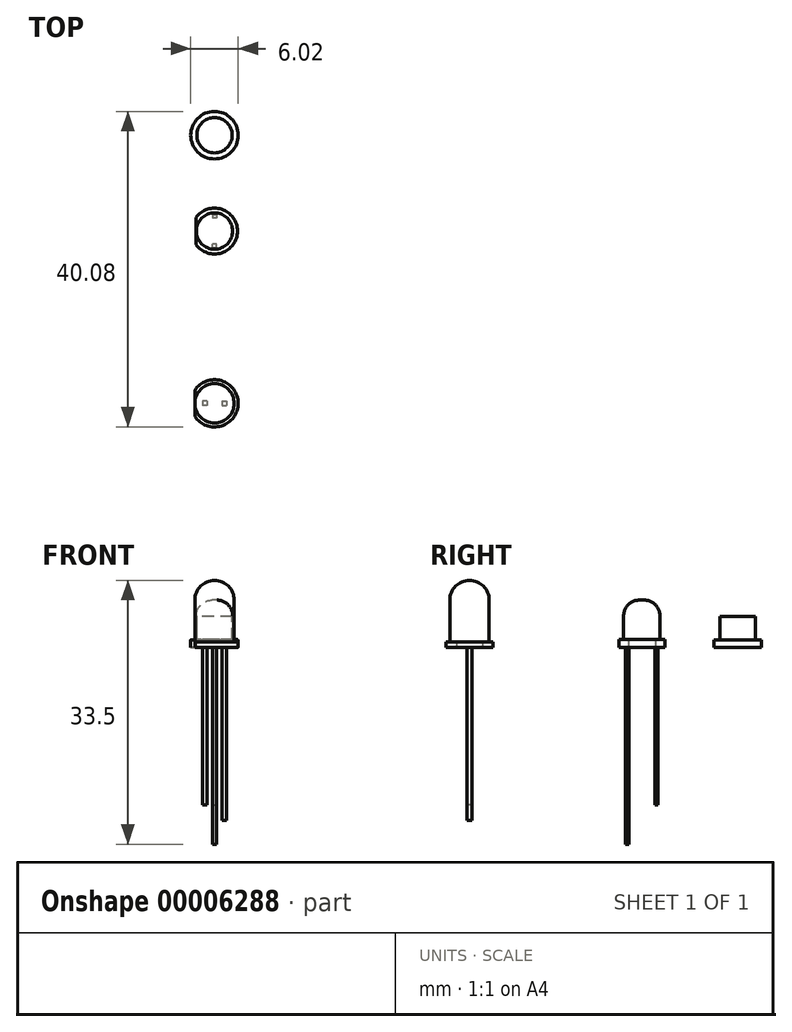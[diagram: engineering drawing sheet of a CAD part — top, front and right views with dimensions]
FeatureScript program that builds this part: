
annotation { "Feature Type Name" : "Feature", "Feature Type Description" : "" }
export const myFeature = defineFeature(function(context is Context, id is Id, definition is map)
    precondition{}
    {
        {
            var Q0;
            Q0=qCreatedBy(makeId("Top.planeOp"),FACE);
            var sketch = newSketch(context, id + "F0", { "sketchPlane" : qUnion([Q0])});
            skCircle(sketch, "E0", {"center": v(0, 0) * mm, "radius": 2.5 * mm});
            skSolve(sketch);
        }
        {
            var Q0;
            Q0 = qSketchRegion(id + "F0", true);
            extrude(context, id + "F1", {"entities" : qUnion([Q0]), "depth" : 6 * mm});
        }
        {
            var Q0;
            Q0=makeQuery(id+"F1.opExtrude","CAP_FACE",FACE,{"disambiguationData":[OSD([sQuery(id+"F0.wireOp",EDGE,"E0")])],"isStart":false});
            var sketch = newSketch(context, id + "F2", { "sketchPlane" : qUnion([Q0])});
            skLineSegment(sketch, "E1", {"start": v(0, -2.5) * mm, "end": v(0, 2.5) * mm});
            skArc(sketch, "E2", {"start": v(0, 2.5) * mm, "mid": v(-2.5, 0) * mm, "end": v(0, -2.5) * mm});
            skSolve(sketch);
        }
        {
            var Q0;
            Q0 = qSketchRegion(id + "F2", true);
            var Q1;
            Q1=sQuery(id+"F2.wireOp",EDGE,"E1");
            revolve(context, id + "F3", {"operationType" : NewBodyOperationType.ADD, "entities" : qUnion([Q0]), "axis" : qUnion([Q1]), "revolveType" : RevolveType.FULL});
        }
        {
            var Q0;
            Q0=makeQuery(id+"F1.opExtrude","CAP_FACE",FACE,{"disambiguationData":[OSD([sQuery(id+"F0.wireOp",EDGE,"E0")])],"isStart":true});
            var sketch = newSketch(context, id + "F4", { "sketchPlane" : qUnion([Q0])});
            skArc(sketch, "E3.0", {"start": v(-2.5, -1.66) * mm, "mid": v(3, 0) * mm, "end": v(-2.5, 1.66) * mm});
            skLineSegment(sketch, "E4", {"start": v(-2.5, -1.66) * mm, "end": v(-2.5, 1.66) * mm});
            skSolve(sketch);
        }
        {
            var Q0;
            Q0 = qSketchRegion(id + "F4", true);
            extrude(context, id + "F5", {"entities" : qUnion([Q0]), "operationType" : NewBodyOperationType.ADD, "oppositeDirection" : true, "depth" : .7 * mm});
        }
        {
            var Q0;
            Q0=makeQuery(id+"F5.boolean.opBoolean","MERGE",FACE,{"derivedFrom":[makeQuery(id+"F1.opExtrude","CAP_FACE",FACE,{"disambiguationData":[OSD([sQuery(id+"F0.wireOp",EDGE,"E0")])],"isStart":true}),makeQuery(id+"F5.opExtrude","CAP_FACE",FACE,{"disambiguationData":[OSD([sQuery(id+"F4.wireOp",EDGE,"E3.0"),sQuery(id+"F4.wireOp",EDGE,"E4")])],"isStart":true})]});
            var sketch = newSketch(context, id + "F6", { "sketchPlane" : qUnion([Q0])});
            skLineSegment(sketch, "E5.rect.bottom", {"start": v(0.95, -0.3) * mm, "end": v(1.55, -0.3) * mm});
            skLineSegment(sketch, "E5.rect.top", {"start": v(0.95, 0.3) * mm, "end": v(1.55, 0.3) * mm});
            skLineSegment(sketch, "E5.rect.left", {"start": v(0.95, -0.3) * mm, "end": v(0.95, 0.3) * mm});
            skLineSegment(sketch, "E5.rect.right", {"start": v(1.55, -0.3) * mm, "end": v(1.55, 0.3) * mm});
            skPoint(sketch, "E5.rect.middle", {"position": v(1.25, 0) * mm});
            skLineSegment(sketch, "E6.rect.bottom", {"start": v(-0.95, -0.3) * mm, "end": v(-1.55, -0.3) * mm});
            skLineSegment(sketch, "E6.rect.top", {"start": v(-0.95, 0.3) * mm, "end": v(-1.55, 0.3) * mm});
            skLineSegment(sketch, "E6.rect.left", {"start": v(-0.95, -0.3) * mm, "end": v(-0.95, 0.3) * mm});
            skLineSegment(sketch, "E6.rect.right", {"start": v(-1.55, -0.3) * mm, "end": v(-1.55, 0.3) * mm});
            skPoint(sketch, "E6.rect.middle", {"position": v(-1.25, 0) * mm});
            skLineSegment(sketch, "E7", {"start": v(1.55, -0.3) * mm, "end": v(0.95, 0.3) * mm, "construction": true});
            skLineSegment(sketch, "E8", {"start": v(1.55, 0.3) * mm, "end": v(0.95, -0.3) * mm, "construction": true});
            skLineSegment(sketch, "E9", {"start": v(-0.95, -0.3) * mm, "end": v(-1.55, 0.3) * mm, "construction": true});
            skLineSegment(sketch, "E10", {"start": v(-0.95, 0.3) * mm, "end": v(-1.55, -0.3) * mm, "construction": true});
            skLineSegment(sketch, "E11", {"start": v(1.25, 0) * mm, "end": v(-1.25, 0) * mm, "construction": true});
            skSolve(sketch);
        }
        {
            var Q0;
            Q0 = qSketchRegion(id + "F6", true);
            extrude(context, id + "F7", {"entities" : qUnion([Q0]), "operationType" : NewBodyOperationType.ADD, "depth" : 20 * mm});
        }
        {
            var Q0;
            Q0=makeQuery(id+"F7.opExtrude","CAP_FACE",FACE,{"disambiguationData":[OSD([sQuery(id+"F6.wireOp",EDGE,"E5.rect.bottom"),sQuery(id+"F6.wireOp",EDGE,"E5.rect.top"),sQuery(id+"F6.wireOp",EDGE,"E5.rect.left"),sQuery(id+"F6.wireOp",EDGE,"E5.rect.right")])],"isStart":false});
            extrude(context, id + "F8", {"entities" : qUnion([Q0]), "operationType" : NewBodyOperationType.ADD, "depth" : 2 * mm});
        }
        {
            var Q0;
            Q0=qCreatedBy(makeId("Top.planeOp"),FACE);
            var sketch = newSketch(context, id + "F9", { "sketchPlane" : qUnion([Q0])});
            skCircle(sketch, "E12", {"center": v(7.44, 15.47) * mm, "radius": 4.08 * mm});
            skSolve(sketch);
        }
        {
            var Q0;
            Q0=makeQuery(id+"F9.imprint","IMPRINT",FACE,{"disambiguationData":[TD([[makeQuery(id+"F9.imprint","IMPRINT",EDGE,{"derivedFrom":sQuery(id+"F9.wireOp",EDGE,"E12")}),1.0]])]});
            extrude(context, id + "F10", {"entities" : qUnion([Q0]), "depth" : 0.62 * mm});
        }
        {
            var Q0;
            Q0=makeQuery(id+"F10.opExtrude","SWEPT_BODY",BODY,{"disambiguationData":[OSD([sQuery(id+"F9.wireOp",EDGE,"E12")])]});
            deleteBodies(context, id + "F11", {"entities" : qUnion([Q0])});
        }
        {
            var Q0;
            Q0=qCreatedBy(makeId("Top.planeOp"),FACE);
            var sketch = newSketch(context, id + "F12", { "sketchPlane" : qUnion([Q0])});
            skCircle(sketch, "E13", {"center": v(0, 21.89) * mm, "radius": 2.91 * mm});
            skSolve(sketch);
        }
        {
            var Q0;
            Q0 = qSketchRegion(id + "F12", true);
            extrude(context, id + "F13", {"entities" : qUnion([Q0]), "depth" : 1 * mm});
        }
        {
            var Q0;
            Q0=makeQuery(id+"F13.opExtrude","CAP_FACE",FACE,{"disambiguationData":[OSD([sQuery(id+"F12.wireOp",EDGE,"E13")])],"isStart":false});
            var sketch = newSketch(context, id + "F14", { "sketchPlane" : qUnion([Q0])});
            skCircle(sketch, "E14", {"center": v(0, 21.89) * mm, "radius": 2.3 * mm});
            skSolve(sketch);
        }
        {
            var Q0;
            Q0 = qSketchRegion(id + "F14", true);
            extrude(context, id + "F15", {"entities" : qUnion([Q0]), "operationType" : NewBodyOperationType.ADD, "depth" : 5 * mm});
        }
        {
            var Q0;
            Q0=makeQuery(id+"F15.opExtrude","CAP_EDGE",EDGE,{"disambiguationData":[OSD([sQuery(id+"F14.wireOp",EDGE,"E14")])],"isStart":false});
            fillet(context, id + "F16", {"entities" : qUnion([Q0]), "radius" : 2 * mm, "tangentPropagation" : true, "allowEdgeOverflow" : false});
        }
        {
            var Q0;
            Q0=makeQuery(id+"F13.opExtrude","CAP_FACE",FACE,{"disambiguationData":[OSD([sQuery(id+"F12.wireOp",EDGE,"E13")])],"isStart":true});
            var sketch = newSketch(context, id + "F17", { "sketchPlane" : qUnion([Q0])});
            skLineSegment(sketch, "E15.rect.bottom", {"start": v(-0.26, -23.96) * mm, "end": v(0.26, -23.96) * mm});
            skLineSegment(sketch, "E15.rect.left", {"start": v(-0.26, -23.96) * mm, "end": v(-0.26, -23.54) * mm});
            skLineSegment(sketch, "E15.rect.right", {"start": v(0.26, -23.96) * mm, "end": v(0.26, -23.54) * mm});
            skPoint(sketch, "E15.rect.middle", {"position": v(0, -21.89) * mm});
            skLineSegment(sketch, "E16", {"start": v(0.26, -23.54) * mm, "end": v(-0.26, -23.54) * mm});
            skLineSegment(sketch, "E17", {"start": v(-1.36, -21.89) * mm, "end": v(2.2, -21.89) * mm, "construction": true});
            skPoint(sketch, "E15.rect.top.end.orphan", {"position": v(0.26, -19.81) * mm});
            skPoint(sketch, "E15.rect.top.start.orphan", {"position": v(-0.26, -19.81) * mm});
            skLineSegment(sketch, "E18.0.MirrorCS", {"start": v(-0.26, -19.81) * mm, "end": v(-0.26, -20.23) * mm});
            skLineSegment(sketch, "E18.1.MirrorCS", {"start": v(-0.26, -19.81) * mm, "end": v(0.26, -19.81) * mm});
            skLineSegment(sketch, "E18.2.MirrorCS", {"start": v(0.26, -19.81) * mm, "end": v(0.26, -20.23) * mm});
            skLineSegment(sketch, "E18.3.MirrorCS", {"start": v(0.26, -20.23) * mm, "end": v(-0.26, -20.23) * mm});
            skSolve(sketch);
        }
        {
            var Q0;
            Q0=makeQuery(id+"F17.imprint","IMPRINT",FACE,{"disambiguationData":[TD([[makeQuery(id+"F17.imprint","IMPRINT",EDGE,{"derivedFrom":sQuery(id+"F17.wireOp",EDGE,"E18.0.MirrorCS")}),1.0]])]});
            extrude(context, id + "F18", {"entities" : qUnion([Q0]), "operationType" : NewBodyOperationType.ADD, "depth" : 25 * mm});
        }
        {
            var Q0;
            Q0=makeQuery(id+"F17.imprint","IMPRINT",FACE,{"disambiguationData":[TD([[makeQuery(id+"F17.imprint","IMPRINT",EDGE,{"derivedFrom":sQuery(id+"F17.wireOp",EDGE,"E15.rect.bottom")}),-1.0]])]});
            var sketch = newSketch(context, id + "F19", { "sketchPlane" : qUnion([Q0])});
            skLineSegment(sketch, "E19.0", {"start": v(-0.26, -23.96) * mm, "end": v(-0.26, -23.54) * mm});
            skLineSegment(sketch, "E20.0", {"start": v(-0.26, -23.96) * mm, "end": v(0.26, -23.96) * mm});
            skLineSegment(sketch, "E20.1", {"start": v(0.26, -23.96) * mm, "end": v(0.26, -23.54) * mm});
            skLineSegment(sketch, "E20.2", {"start": v(0.26, -23.54) * mm, "end": v(-0.26, -23.54) * mm});
            skSolve(sketch);
        }
        {
            var Q0;
            Q0 = qSketchRegion(id + "F19", true);
            extrude(context, id + "F20", {"entities" : qUnion([Q0]), "operationType" : NewBodyOperationType.ADD, "depth" : 20 * mm});
        }
        {
            var Q0;
            Q0=makeQuery(id+"F17.imprint","IMPRINT",FACE,{"disambiguationData":[TD([[makeQuery(id+"F17.imprint","IMPRINT",EDGE,{"derivedFrom":sQuery(id+"F17.wireOp",EDGE,"E15.rect.bottom")}),-1.0]])]});
            var sketch = newSketch(context, id + "F21", { "sketchPlane" : qUnion([Q0])});
            skArc(sketch, "E21.0", {"start": v(-2.35, -20.16) * mm, "mid": v(-2.91, -21.89) * mm, "end": v(-2.35, -23.6) * mm});
            skLineSegment(sketch, "E22", {"start": v(-2.35, -23.6) * mm, "end": v(-2.35, -20.16) * mm});
            skSolve(sketch);
        }
        {
            var Q0;
            Q0 = qSketchRegion(id + "F21", true);
            extrude(context, id + "F22", {"entities" : qUnion([Q0]), "operationType" : NewBodyOperationType.REMOVE, "oppositeDirection" : true, "depth" : 25 * mm});
        }
        {
            var Q0;
            Q0=qCreatedBy(makeId("Right.planeOp"),FACE);
            var sketch = newSketch(context, id + "F23", { "sketchPlane" : qUnion([Q0])});
            skLineSegment(sketch, "E23", {"start": v(31.05, 0) * mm, "end": v(31.05, 0.96) * mm});
            skLineSegment(sketch, "E24", {"start": v(31.05, 0.96) * mm, "end": v(31.82, 0.96) * mm});
            skLineSegment(sketch, "E25", {"start": v(31.82, 0.96) * mm, "end": v(31.82, 3.91) * mm});
            skLineSegment(sketch, "E26", {"start": v(31.82, 3.91) * mm, "end": v(34.06, 3.91) * mm});
            skLineSegment(sketch, "E27", {"start": v(34.06, 3.91) * mm, "end": v(34.06, 0) * mm});
            skLineSegment(sketch, "E28", {"start": v(34.06, 0) * mm, "end": v(31.05, 0) * mm});
            skLineSegment(sketch, "E29", {"start": v(34.06, 3.91) * mm, "end": v(34.06, -6.33) * mm, "construction": true});
            skSolve(sketch);
        }
        {
            var Q0;
            Q0=makeQuery(id+"F23.imprint","IMPRINT",FACE,{"disambiguationData":[TD([[makeQuery(id+"F23.imprint","IMPRINT",EDGE,{"derivedFrom":sQuery(id+"F23.wireOp",EDGE,"E23")}),-1.0]])]});
            var Q1;
            Q1=sQuery(id+"F23.wireOp",EDGE,"E29");
            revolve(context, id + "F24", {"entities" : qUnion([Q0]), "axis" : qUnion([Q1]), "revolveType" : RevolveType.FULL});
        }
    });
